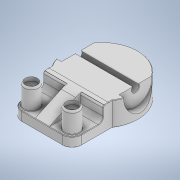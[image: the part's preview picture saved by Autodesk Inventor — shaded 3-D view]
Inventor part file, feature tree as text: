
AUTODESK INVENTOR PART (.ipt)
format: ipt  version: 2021 (Build 250183000, 183)  size: 376,320 bytes
history: native  units: in
note: dims shown in document units (in); Inventor stores cm internally (conversion verified against a paired STEP export)
features: extrude x10, sketch x10, fillet x9, plane x4
ambient origin geometry x8: Origin, YZ Plane, XZ Plane, XY Plane, X Axis, Y Axis, Z Axis, Center Point
bodies: Solid1 (feature_tree)
feature tree (33):
  extrude  "Extrusion1"  Depth=0.9843in
  plane  "Work Plane1"
  extrude  "Extrusion2"  Depth=0.3937in TaperAngle=0.0deg
  plane  "Work Plane2"
  extrude  "Extrusion3"  Depth=0.5906in
  extrude  "Extrusion4"  Depth=0.0787in
  extrude  "Extrusion5"  [1 undecoded]
  extrude  "Extrusion6"  Depth=0.0787in
  plane  "Work Plane3"
  extrude  "Extrusion7"  Depth=0.1181in TaperAngle=0.0deg
  extrude  "Extrusion8"  Depth=0.0787in
  plane  "Work Plane4"
  extrude  "Extrusion9"  Depth=0.1575in
  fillet  "Fillet1"  Radius=0.2362in
  fillet  "Fillet2"  [1 undecoded]
  fillet  "Fillet3"  Radius=0.4724in
  fillet  "Fillet4"  Radius=0.4724in
  fillet  "Fillet5"  [1 undecoded]
  fillet  "Fillet6"  Radius=0.1575in
  extrude  "Extrusion10"  Depth=0.2362in
  fillet  "Fillet7"  Radius=0.1575in
  fillet  "Fillet8"  Radius=0.1575in
  fillet  "Fillet9"  Radius=0.2362in
  sketch  "Sketch1"  dims[d0=1.1811in d1=0.9843in]
  sketch  "Sketch2"  dims[d2=0.7874in d4=0.3937in d5=0.0in]
  sketch  "Sketch3"  dims[d6=0.5906in d7=0.3543in]
  sketch  "Sketch4"  dims[d8=0.0787in d9=0.5512in]
  sketch  "Sketch5"  dims[d10=0.1181in d11=0.0in d12=-1.1811in]
  sketch  "Sketch6"  dims[d13=0.3543in d14=0.0787in]
  sketch  "Sketch7"  dims[d15=0.5512in d16=0.1181in d17=0.0in]
  sketch  "Sketch8"  dims[d18=0.3543in d19=0.0787in]
  sketch  "Sketch9"  dims[d20=0.1181in d21=0.4724in d22=0.2362in d23=0.0in d24=0.0in d25=0.4724in d26=0.0in d27=0.4724in d28=0.0in d29=0.0in d30=0.1575in]
  sketch  "Sketch10"  dims[d31=0.1575in d32=0.2362in d33=0.1575in d34=0.1575in d35=0.2362in d36=0.3386in d37=0.0in d38=0.3386in d39=0.0in d40=0.0in d41=0.1969in d42=0.1969in d43=0.1024in d44=0.0in d45=0.0394in d46=0.0787in d47=0.0394in d48=0.3937in d49=0.0079in d50=0.0079in d51=0.3937in d52=0.0394in d53=0.0in d54=0.0079in d55=0.0079in d56=0.0118in]
note: 3 required parameter values undecoded (feature->parameter linkage not recoverable at this tier; creation-order binding heuristic only, values carry confidence <= 0.55)
